# Revit family: Bosch_MechanicalEquipment_HotWaterCondensingBoiler_UNI3000F
name_source: partatom
category: Mechanical Equipment
revit_build: Autodesk Revit 2016 (Build: 20151007_0715(x64)
units: mm (PartAtom-declared; Revit-internal decimal feet)

## family parameters
Always vertical = Yes
Cut with Voids When Loaded = No
OmniClass Number = 23.75.00.00
OmniClass Title = Climate Control (HVAC)
Part Type = Normal
Room Calculation Point = No
Round Connector Dimension = Use Radius
Shared = No
Work Plane-Based = No

## types (9) — shared parameters
6Monthly = Mid service if using Oil 35 sec
AccessClearanceBottom = 0
AccessClearanceFront = 2500
AccessClearanceLeft = 250 (depending on door handing)
AccessClearanceRear = 1000
AccessClearanceRight = Burner length + 250
AccessClearanceTop = 0
AccessFront = 2500 mm
AccessLeft = 250 mm  [stored 0.82021 ft]
AccessRear = 1000 mm
AccessRight = 250 mm  [stored 0.82021 ft]
Annually = Annual Service
Assembly Code = D3020100
AssetType = Fixed
BMSLinks = Yes
BespokeTimeframe = No
BuildingRegulationsSeasonalEfficiency = 85.3
BurnerConfiguration = Separate
BurnerDepth = 555 mm
CEApproval = CE1015-13
ClassificationName = Uniclass2015
ClassificationValue = Pr_60_60_08_25
Color = RAL 3020 Red
Colour = RAL 3020 red
CondensateDrainType = Plain
Configuration = Single Boiler
Constituents = Stainless steel, steel, polymers
ControlOptions = Unset
ControlType = External
D(EL) = 20 mm  [stored 0.0656168 ft]
Daily = No
Description = Available in 9 outputs the Bosch Uni 3000 F high-efficiency steel boiler utilises reverse flame technology to deliver hot water to heating systems with efficiency up to 93% (NCV)*.
DocumentationInstallationGuide = https://specifi.bimstore.co.uk
DocumentationLiterature = https://specifi.bimstore.co.uk
DoorPanelOffset = 61 mm  [stored 0.200131 ft]
DrainConnectionType = Threaded
DrainSize = 16 mm  [stored 0.0524934 ft]
DurationUnit = Years
ErPEnergyLabel = N
Expected Life = 20-30
ExpectedLife = 25
ExternalMaterial = Steel
Features = Floor standing high efficiency boiler
Finish = Paint
FlowAndReturnConnectionType = Flanged
FlueOrAirIntakeClassification = B23
Frequency = 50
FuelConnectionSize = dependent on burner
FuelConnectionType = Threaded
H(EL) = 100 mm  [stored 0.328084 ft]
HeatExchangerMaterial = Steel
HeaterOperation = ????
IPRating = dependent on burner used
IfcExportAs = IfcBoiler
IfcExportType = IfcBoilerTypeEnum.WATER
Interlocks = Yes
Keynote = T20/380
MaintenanceRequired0-300Hrs = No
MaintenanceRequired1001-2000Hrs = No
MaintenanceRequired2001-4000Hrs = No
MaintenanceRequired301-600Hrs = No
MaintenanceRequired4001-8000Hrs = No
MaintenanceRequired601-1000Hrs = No
MaintenanceRequired8001-12000Hrs = No
Manufacturer = Bosch Thermotechnology
ManufacturerName = Bosch Thermotechnology
Material = Steel
MaximumGasInletPressure = 100 (dependent on gas train used)
MaximumOilInletPressure = 400
MaximumOperatingPressure = 6
MinimumOilInletPressure = -0.40 (for twin pipe circuits)
MinimumOperatingPressure = 0.8
Model = UNI 3000F - Hot Water Boiler
ModelReference = UNI 3000F - Hot Water Boiler
Monthly = No
Mounting = Floor Standing
NBSDescription = Dual fuel fired steel shell boilers
NBSObjectName = Bosch - Dual fuel fired steel shell boilers
NBSReference = 90-40-05/320
NominalOilInletPressure = 50
O&MManual = http://www.bosch-industrial.co.uk
PlateHeadWidth = 300 mm
PrimaryFuel = Gas - NG
ProductLiterature = http://www.bosch-industrial.co.uk
ProductRange = Uni 3000F
ProductionYear = 2018
Quaterly = No
RatedCriteria = 80/60
RatedEfficiencyAtFullLoad = 91.8
RatedEfficiencyAtPartLoad = 95.3
ReferencedStandard = BS EN
SafetyValveConnectionType = Flanged
SecondaryFuel = Oil - 35/sec
Shape = Cylindrical (Horizontal)
SupplyPhase = 1ph - controls 3ph - burner
TurndownRatio = dependent on burner used
Type = Space Heating
URL = http://www.bosch-industrial.co.uk
Voltage = 230 - controls 400 - burner
WarrantyDurationLabor = 0
WarrantyDurationParts = 0
WarrantyDurationUnit = Years
WarrantyID = Serial number and end user registration
Weekly = System pressure check
_BSBibleVersion = 15
_CurrentRevision = 2
_DistributedBy = www.bimstore.co.uk
zero-valued in all types: AccessTop, _BimSpecGuid

## per-type parameters (varying)
- 420kW: A(1)=450 mm; A(2)=365 mm; A(3)=516 mm; B(G)=1040 mm; B(GR)=570 mm; BIMObjectName=Bosch_MechanicalEquipment_HotWaterCondensingBoiler_UNI3000F_420kW; BaseNotch1=255 mm; BaseNotch2=290 mm; BurnerLength=840 mm; BurnerWidth=511 mm; CylinderCentre=614 mm; CylinderDia=491 mm; D(AA)=300 mm; D(AA)Calc=150 mm; DoorDia=445 mm  [stored 1.45997 ft]; DoorPanelSize=383 mm  [stored 1.25656 ft]; DoorSplayHeight=550 mm; DoorType=Support Plate : 500kW; DrainConnectionSize=R 1 1/4"; FlowAndReturnConnectionSize=DN 100; FlowConnectionSize=40 mm; FlueConnectionSize=300 mm; FlueSize=125 mm  [stored 0.410105 ft]; FullLoadCurrent=2.8 (dependent on burner used); FuseRating=10; GasConsumptionRate=56; GrossWeight=1474.00 kg; H=1430 mm; H(AA)=662 mm; H(K)=1210 mm; L(G)=2075 mm; L(GR)=1503 mm; MaximumPowerConsumption=1400 (dependent on burner used); MinimumGasInletPressure=128 Gas 140 Oil (dependent on burner used); MinimumPowerConsumption=dependent on burner used; NominalGasInletPressure=20; NominalHeight=1430 mm; NominalLength=2075 mm; NominalWidth=1040 mm; OilConsumptionRate=46.1; Overall Height=1430; Overall Length=2075; Overall Width=1040; ProductModelNumber=500kW; RatedOutput=421 - 500; ReturnConnectionSize=40 mm; SafetyConnectionSize=25 mm  [stored 0.082021 ft]; SafetyValveConnectionSize=DN 50; ShippingWeight=1040.00 kg; Size=2075x1040x1430mm; SoundPressureLevel=75 (dependant on burner); StartingCurrent=4.8 (dependent on burner used); SupportPlateDiaCalc=503 mm  [stored 1.65026 ft]; WaterContent=434
- 500kW: A(1)=450 mm; A(2)=365 mm; A(3)=516 mm; B(G)=1040 mm; B(GR)=570 mm; BIMObjectName=Bosch_MechanicalEquipment_HotWaterCondensingBoiler_UNI3000F_500kW; BaseNotch1=255 mm; BaseNotch2=290 mm; BurnerLength=840 mm; BurnerWidth=511 mm; CylinderCentre=614 mm; CylinderDia=491 mm; D(AA)=300 mm; D(AA)Calc=150 mm; DoorDia=445 mm  [stored 1.45997 ft]; DoorPanelSize=383 mm  [stored 1.25656 ft]; DoorSplayHeight=550 mm; DoorType=Support Plate : 500kW; DrainConnectionSize=R 1 1/4"; FlowAndReturnConnectionSize=DN 100; FlowConnectionSize=50 mm; FlueConnectionSize=300 mm; FlueSize=150 mm; FullLoadCurrent=2.8 (dependent on burner used); FuseRating=10; GasConsumptionRate=56; GrossWeight=1474.00 kg; H=1430 mm; H(AA)=662 mm; H(K)=1210 mm; L(G)=2075 mm; L(GR)=1503 mm; MaximumPowerConsumption=1400 (dependent on burner used); MinimumGasInletPressure=128 Gas 140 Oil (dependent on burner used); MinimumPowerConsumption=dependent on burner used; NominalGasInletPressure=20; NominalHeight=1430 mm; NominalLength=2075 mm; NominalWidth=1040 mm; OilConsumptionRate=46.1; Overall Height=1430; Overall Length=2075; Overall Width=1040; ProductModelNumber=500kW; RatedOutput=421 - 500; ReturnConnectionSize=50 mm; SafetyConnectionSize=25 mm  [stored 0.082021 ft]; SafetyValveConnectionSize=DN 50; ShippingWeight=1040.00 kg; Size=2075x1040x1430mm; SoundPressureLevel=75 (dependant on burner); StartingCurrent=4.8 (dependent on burner used); SupportPlateDiaCalc=503 mm  [stored 1.65026 ft]; WaterContent=434
- 600kW: A(1)=450 mm; A(2)=365 mm; A(3)=766 mm; B(G)=1040 mm; B(GR)=570 mm; BIMObjectName=Bosch_MechanicalEquipment_HotWaterCondensingBoiler_UNI3000F_600kW; BaseNotch1=355 mm; BaseNotch2=290 mm; BurnerLength=680 mm; BurnerWidth=580 mm; CylinderCentre=614 mm; CylinderDia=491 mm; D(AA)=300 mm; D(AA)Calc=150 mm; DoorDia=445 mm  [stored 1.45997 ft]; DoorPanelSize=383 mm  [stored 1.25656 ft]; DoorSplayHeight=550 mm; DoorType=Support Plate : 600kW; DrainConnectionSize=R 1 1/4"; FlowAndReturnConnectionSize=DN 100; FlowConnectionSize=50 mm; FlueConnectionSize=300 mm; FlueSize=150 mm; FullLoadCurrent=2.8 (dependent on burner used); FuseRating=10; GasConsumptionRate=68; GrossWeight=1652.00 kg; H=1430 mm; H(AA)=662 mm; H(K)=1210 mm; L(G)=2320 mm; L(GR)=1753 mm; MaximumPowerConsumption=1400 (dependent on burner used); MinimumGasInletPressure=17.6; MinimumPowerConsumption=dependent on burner used; NOxEmissions=128 Gas 160 Oil (dependent on burner used); NominalGasInletPressure=20; NominalHeight=1430 mm; NominalLength=2320 mm; NominalWidth=1040 mm; OilConsumptionRate=55.3; Overall Height=1430; Overall Length=2320; Overall Width=1040; ProductModelNumber=600kW; RatedOutput=501 - 600; ReturnConnectionSize=50 mm; SafetyConnectionSize=25 mm  [stored 0.082021 ft]; SafetyValveConnectionSize=DN 50; ShippingWeight=1150.00 kg; Size=2320x1040x1430mm; SoundPressureLevel=75 (dependant on burner); StartingCurrent=4.8 (dependent on burner used); SupportPlateDiaCalc=503 mm  [stored 1.65026 ft]; WaterContent=502
- 730kW: A(1)=620 mm; A(2)=350 mm  [stored 1.14829 ft]; A(3)=541 mm  [stored 1.77493 ft]; B(G)=1040 mm; B(GR)=650 mm; BIMObjectName=Bosch_MechanicalEquipment_HotWaterCondensingBoiler_UNI3000F_730kW; BaseNotch1=335 mm; BaseNotch2=490 mm; BurnerLength=840 mm; BurnerWidth=527 mm; CylinderCentre=670 mm; CylinderDia=542 mm; D(AA)=350 mm  [stored 1.14829 ft]; D(AA)Calc=175 mm  [stored 0.574147 ft]; DoorDia=496 mm; DoorPanelSize=434 mm; DoorSplayHeight=600 mm; DoorType=Support Plate : 730kW; DrainConnectionSize=R 1 1/4"; FlowAndReturnConnectionSize=DN 125; FlowConnectionSize=63 mm; FlueConnectionSize=350 mm  [stored 1.14829 ft]; FlueSize=175 mm  [stored 0.574147 ft]; FullLoadCurrent=3.4 (dependent on burner used); FuseRating=10; GasConsumptionRate=82; GrossWeight=1967.00 kg; H=1430 mm; H(AA)=727 mm; H(K)=1320 mm; L(G)=2270 mm; L(GR)=1700 mm; MaximumPowerConsumption=1800 (dependent on burner used); MinimumGasInletPressure=16.5; MinimumPowerConsumption=dependent on burner used; NOxEmissions=125 Gas 160 Oil (dependent on burner used); NominalGasInletPressure=20; NominalHeight=1430 mm; NominalLength=2270 mm; NominalWidth=1040 mm; OilConsumptionRate=67.1; Overall Height=1430; Overall Length=2270; Overall Width=1040; ProductModelNumber=730kW; RatedOutput=601 - 730; ReturnConnectionSize=63 mm; SafetyConnectionSize=33 mm; SafetyValveConnectionSize=DN 65; ShippingWeight=1360.00 kg; Size=2270x1040x1430mm; SoundPressureLevel=77 (dependant on burner); StartingCurrent=5.9 (dependent on burner used); SupportPlateDiaCalc=554 mm; WaterContent=607
- 820kW: A(1)=620 mm; A(2)=350 mm  [stored 1.14829 ft]; A(3)=541 mm  [stored 1.77493 ft]; B(G)=1040 mm; B(GR)=650 mm; BIMObjectName=Bosch_MechanicalEquipment_HotWaterCondensingBoiler_UNI3000F_820kW; BaseNotch1=435 mm; BaseNotch2=490 mm; BurnerLength=840 mm; BurnerWidth=527 mm; CylinderCentre=670 mm; CylinderDia=542 mm; D(AA)=350 mm  [stored 1.14829 ft]; D(AA)Calc=175 mm  [stored 0.574147 ft]; DoorDia=496 mm; DoorPanelSize=434 mm; DoorSplayHeight=600 mm; DoorType=Support Plate : 820kW; DrainConnectionSize=R 1 1/4"; FlowAndReturnConnectionSize=DN 125; FlowConnectionSize=63 mm; FlueConnectionSize=350 mm  [stored 1.14829 ft]; FlueSize=175 mm  [stored 0.574147 ft]; FullLoadCurrent=3.4 (dependent on burner used); FuseRating=10; GasConsumptionRate=92; GrossWeight=2135.00 kg; H=1430 mm; H(AA)=727 mm; H(K)=1320 mm; L(G)=2469 mm; L(GR)=1900 mm; MaximumPowerConsumption=1800 (dependent on burner used); MinimumGasInletPressure=19.1 (depending on gas train used); MinimumPowerConsumption=dependent on burner used; NOxEmissions=70 Gas 160 Oil (dependent on burner used); NominalGasInletPressure=20; NominalHeight=1430 mm; NominalLength=2469 mm; NominalWidth=1040 mm; OilConsumptionRate=75.4; Overall Height=1430; Overall Length=2469; Overall Width=1040; ProductModelNumber=820kW; RatedOutput=731 - 820; ReturnConnectionSize=63 mm; SafetyConnectionSize=33 mm; SafetyValveConnectionSize=DN 65; ShippingWeight=1460.00 kg; Size=2469x1040x1430mm; SoundPressureLevel=79 (dependant on burner); StartingCurrent=5.9 (dependent on burner used); SupportPlateDiaCalc=554 mm; WaterContent=675
- 1040kW: A(1)=620 mm; A(2)=595 mm; A(3)=569 mm; B(G)=1470 mm; B(GR)=820 mm; BIMObjectName=Bosch_MechanicalEquipment_HotWaterCondensingBoiler_UNI3000F_1040kW; BaseNotch1=411 mm; BaseNotch2=490 mm; BurnerLength=840 mm; BurnerWidth=527 mm; CylinderCentre=725 mm; CylinderDia=602 mm; D(AA)=350 mm  [stored 1.14829 ft]; D(AA)Calc=175 mm  [stored 0.574147 ft]; DoorDia=556 mm; DoorPanelSize=494 mm; DoorSplayHeight=702 mm; DoorType=Support Plate : 1040kW; DrainConnectionSize=R 1 1/4"; FlowAndReturnConnectionSize=DN 125; FlowConnectionSize=63 mm; FlueConnectionSize=350 mm  [stored 1.14829 ft]; FlueSize=175 mm  [stored 0.574147 ft]; FullLoadCurrent=3.4 (dependent on burner used); FuseRating=10; GasConsumptionRate=118; GrossWeight=2612.00 kg; H=1475 mm; H(AA)=797 mm; H(K)=1340 mm; L(G)=2600 mm; L(GR)=1960 mm; MaximumPowerConsumption=1800 (dependent on burner used); MinimumGasInletPressure=23.1 (depending on gas train used); MinimumPowerConsumption=dependent on burner used; NOxEmissions=125 Gas 160 Oil (dependent on burner used); NominalGasInletPressure=25; NominalHeight=1475 mm; NominalLength=2600 mm; NominalWidth=1470 mm; OilConsumptionRate=96; Overall Height=1475; Overall Length=2600; Overall Width=1470; ProductModelNumber=1040kW; RatedOutput=821 - 1040; ReturnConnectionSize=63 mm; SafetyConnectionSize=40 mm; SafetyValveConnectionSize=DN 80; ShippingWeight=1790.00 kg; Size=2600x1470x1475mm; SoundPressureLevel=77 (dependant on burner); StartingCurrent=5.9 (dependent on burner used); SupportPlateDiaCalc=614 mm; WaterContent=822
- 1200kW: A(1)=620 mm; A(2)=595 mm; A(3)=870 mm; B(G)=1470 mm; B(GR)=820 mm; BIMObjectName=Bosch_MechanicalEquipment_HotWaterCondensingBoiler_UNI3000F_1200kW; BaseNotch1=562 mm; BaseNotch2=490 mm; BurnerLength=840 mm; BurnerWidth=553 mm; CylinderCentre=725 mm; CylinderDia=602 mm; D(AA)=350 mm  [stored 1.14829 ft]; D(AA)Calc=175 mm  [stored 0.574147 ft]; DoorDia=556 mm; DoorPanelSize=494 mm; DoorSplayHeight=702 mm; DoorType=Support Plate : 1200kW; DrainConnectionSize=R 1 1/4"; FlowAndReturnConnectionSize=DN 125; FlowConnectionSize=63 mm; FlueConnectionSize=350 mm  [stored 1.14829 ft]; FlueSize=175 mm  [stored 0.574147 ft]; FullLoadCurrent=5.1 (dependent on burner used); FuseRating=10; GasConsumptionRate=136; GrossWeight=3012.00 kg; H=1475 mm; H(AA)=797 mm; H(K)=1340 mm; L(G)=2882 mm; L(GR)=2260 mm; MaximumPowerConsumption=2600 (dependent on burner used); MinimumGasInletPressure=43.9 (depending on gas train used); MinimumPowerConsumption=dependent on burner used; NOxEmissions=105 Gas 155 Oil (dependent on burner used); NominalGasInletPressure=50; NominalHeight=1475 mm; NominalLength=2882 mm; NominalWidth=1470 mm; OilConsumptionRate=110.8; Overall Height=1475; Overall Length=2882; Overall Width=1470; ProductModelNumber=1200kW; RatedOutput=1041 - 1200; ReturnConnectionSize=63 mm; SafetyConnectionSize=40 mm; SafetyValveConnectionSize=DN 80; ShippingWeight=2070.00 kg; Size=2882x1470x1475mm; SoundPressureLevel=79 (dependant on burner); StartingCurrent=8.8 (dependent on burner used); SupportPlateDiaCalc=614 mm; WaterContent=942
- 1400kW: A(1)=725 mm; A(2)=725 mm; A(3)=673 mm; B(G)=1610 mm; B(GR)=880 mm; BIMObjectName=Bosch_MechanicalEquipment_HotWaterCondensingBoiler_UNI3000F_1400kW; BaseNotch1=607 mm; BaseNotch2=490 mm; BurnerLength=873 mm; BurnerWidth=732 mm; CylinderCentre=780 mm; CylinderDia=664 mm; D(AA)=400 mm  [stored 1.31234 ft]; D(AA)Calc=200 mm  [stored 0.656168 ft]; DoorDia=618 mm; DoorPanelSize=556 mm; DoorSplayHeight=747 mm; DoorType=Support Plate : 1400kW; DrainConnectionSize=R 1 1/4"; FlowAndReturnConnectionSize=DN 150; FlowConnectionSize=63 mm; FlueConnectionSize=350 mm  [stored 1.14829 ft]; FlueSize=175 mm  [stored 0.574147 ft]; FullLoadCurrent=9.1 (dependent on burner used); FuseRating=20; GasConsumptionRate=158; GrossWeight=3999.00 kg; H=1612 mm; H(AA)=1070 mm; H(K)=1460 mm; L(G)=3050 mm; L(GR)=2316 mm; MaximumPowerConsumption=2600 (dependent on burner used); MinimumGasInletPressure=56.4 (depending on gas train used); MinimumPowerConsumption=dependent on burner used; NOxEmissions=TBC; NominalGasInletPressure=60; NominalHeight=1612 mm; NominalLength=3050 mm; NominalWidth=1610 mm; OilConsumptionRate=129.3; Overall Height=1612; Overall Length=3050; Overall Width=1610; ProductModelNumber=1400kW; RatedOutput=1201 - 1400; ReturnConnectionSize=63 mm; SafetyConnectionSize=40 mm; SafetyValveConnectionSize=DN 80; ShippingWeight=2660.00 kg; Size=3050x1610x1612mm; SoundPressureLevel=79 (dependant on burner); StartingCurrent=15.8 (dependent on burner used); SupportPlateDiaCalc=676 mm; WaterContent=1339
- 1850kW: A(1)=925 mm; A(2)=925 mm; A(3)=670 mm; B(G)=1730 mm; B(GR)=860 mm; BIMObjectName=Bosch_MechanicalEquipment_HotWaterCondensingBoiler_UNI3000F_1850kW; BaseNotch1=783 mm; BaseNotch2=490 mm; BurnerLength=872 mm; BurnerWidth=732 mm; CylinderCentre=830 mm; CylinderDia=705 mm; D(AA)=400 mm  [stored 1.31234 ft]; D(AA)Calc=200 mm  [stored 0.656168 ft]; DoorDia=659 mm; DoorPanelSize=597 mm; DoorSplayHeight=739 mm; DoorType=Support Plate : 1850kW; DrainConnectionSize=R 1 1/2"; FlowAndReturnConnectionSize=DN 200; FlowConnectionSize=63 mm; FlueConnectionSize=400 mm  [stored 1.31234 ft]; FlueSize=175 mm  [stored 0.574147 ft]; FullLoadCurrent=21.3 (dependent on burner used); FuseRating=160; GasConsumptionRate=209; GrossWeight=5255.00 kg; H=1730 mm; H(AA)=1145 mm; H(K)=1545 mm; L(G)=3340 mm; L(GR)=2720 mm; MaximumPowerConsumption=6500 (dependent on burner used); MinimumGasInletPressure=50.9 (depending on gas train used); MinimumPowerConsumption=5500; NOxEmissions=(dependant on burner); NominalGasInletPressure=60; NominalHeight=1730 mm; NominalLength=3340 mm; NominalWidth=1730 mm; OilConsumptionRate=170.8; Overall Height=1730; Overall Length=3340; Overall Width=1730; ProductModelNumber=1850kW; RatedOutput=1401 - 1850; ReturnConnectionSize=63 mm; SafetyConnectionSize=40 mm; SafetyValveConnectionSize=DN 100; ShippingWeight=3600.00 kg; Size=3340x1730x1730mm; SoundPressureLevel=(dependant on burner); StartingCurrent=143 (dependent on burner used); SupportPlateDiaCalc=717 mm; WaterContent=1655

note: column(s) folded — value = type name in every type: ModelNumber, Type Comments, TypeName

note: [stored X ft] marks values corroborated as IEEE doubles in the binary element streams (Revit-internal decimal feet)

## geometry (parser evidence)
native form markers: Blend x8, Sweep x27
no freeform markers — native parametric forms only
